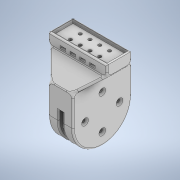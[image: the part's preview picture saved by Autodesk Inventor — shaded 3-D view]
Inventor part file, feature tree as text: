
AUTODESK INVENTOR PART (.ipt)
format: ipt  version: 2022 (Build 260153000, 153)  size: 623,616 bytes
history: native  units: mm
features: sketch x11, extrude x10, other x6, projected_geometry x4, chamfer x2, loft x1, fillet x1
ambient origin geometry x8: Origin, YZ Plane, XZ Plane, XY Plane, X Axis, Y Axis, Z Axis, Center Point
bodies: Body1 (feature_tree)
feature tree (35):
  other  "Твердое тело1"
  extrude  "Выдавливание1"  Depth=20.0mm
  extrude  "Выдавливание2"  Depth=55.6mm
  extrude  "Выдавливание4"  Depth=2.5mm
  extrude  "Выдавливание9"  Depth=2.0mm
  other  "РабПлоскость2"
  extrude  "Выдавливание10"  Depth=2.0mm TaperAngle=0.0deg
  extrude  "Выдавливание11"  Depth=2.0mm
  other  "РабПлоскость3"
  loft  "Лофт1"
  other  "РабПлоскость5"
  sketch  "Эскиз18"
  other  "РабПлоскость6"
  extrude  "Выдавливание14"  Depth=5.0mm TaperAngle=0.0deg
  extrude  "Выдавливание15"  Depth=14.0mm
  other  "РабПлоскость7"
  sketch  "Эскиз20"
  chamfer  "Фаска1"  Distance=40.0mm Angle=360.0deg
  extrude  "Выдавливание17"  Depth=3.2mm
  extrude  "Выдавливание18"  Depth=6.2mm
  chamfer  "Фаска2"  Distance=14.0mm
  fillet  "Сопряжение6"  [1 undecoded]
  sketch  "Эскиз1"
  sketch  "Эскиз2"
  projected_geometry  "Спроецированная петля1"
  sketch  "Эскиз12"
  projected_geometry  "Спроецированная петля4"
  sketch  "Эскиз13"
  sketch  "Эскиз14"
  projected_geometry  "Спроецированная петля5"
  sketch  "Эскиз15"
  sketch  "Эскиз17"
  sketch  "Эскиз19"
  sketch  "Эскиз21"
  projected_geometry  "Спроецированная петля6"
note: 1 required parameter value undecoded (feature->parameter linkage not recoverable at this tier; creation-order binding heuristic only, values carry confidence <= 0.55)
